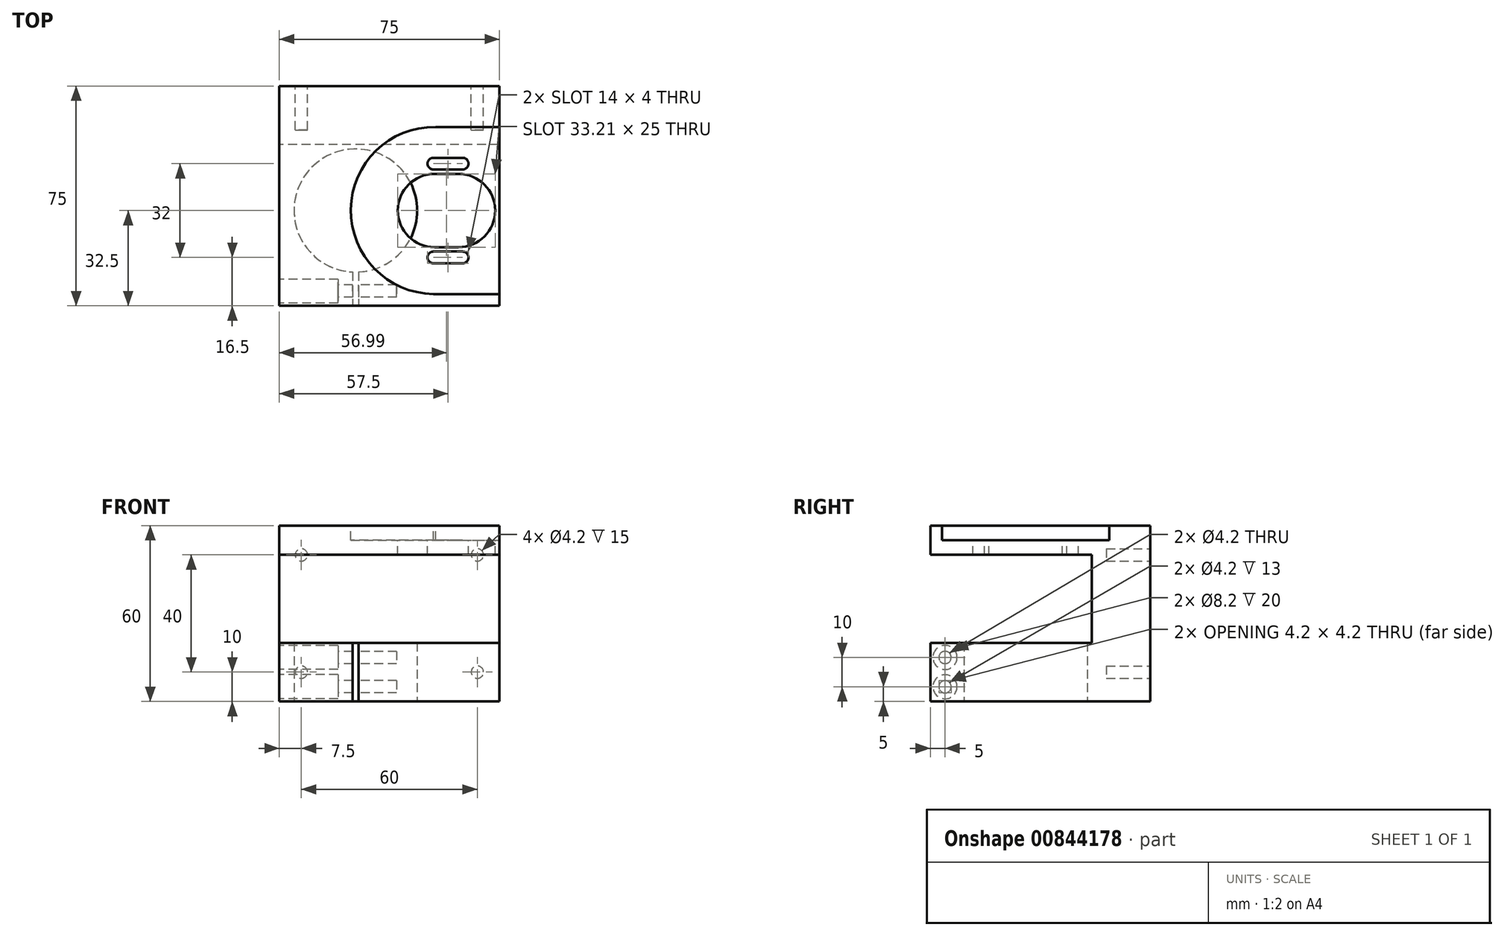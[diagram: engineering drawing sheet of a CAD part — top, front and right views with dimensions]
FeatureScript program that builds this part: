
annotation { "Feature Type Name" : "Feature", "Feature Type Description" : "" }
export const myFeature = defineFeature(function(context is Context, id is Id, definition is map)
    precondition{}
    {
        {
            var Q0;
            Q0=qCreatedBy(makeId("Top.planeOp"),FACE);
            var sketch = newSketch(context, id + "F0", { "sketchPlane" : qUnion([Q0])});
            skLineSegment(sketch, "E0.bottom", {"start": v(37.5, -37.5) * mm, "end": v(-37.5, -37.5) * mm});
            skLineSegment(sketch, "E0.top", {"start": v(37.5, 37.5) * mm, "end": v(-37.5, 37.5) * mm});
            skLineSegment(sketch, "E0.left", {"start": v(37.5, -37.5) * mm, "end": v(37.5, 37.5) * mm});
            skLineSegment(sketch, "E0.right", {"start": v(-37.5, -37.5) * mm, "end": v(-37.5, 37.5) * mm});
            skPoint(sketch, "E0.middle", {"position": v(0, 0) * mm});
            skLineSegment(sketch, "E1", {"start": v(-37.5, 0) * mm, "end": v(37.5, 0) * mm, "construction": true});
            skSolve(sketch);
        }
        {
            var Q0;
            Q0=makeQuery(id+"F0.imprint","IMPRINT",FACE,{"disambiguationData":[TD([[makeQuery(id+"F0.imprint","IMPRINT",EDGE,{"derivedFrom":sQuery(id+"F0.wireOp",EDGE,"E0.bottom")}),-1.0]])]});
            extrude(context, id + "F1", {"entities" : qUnion([Q0]), "depth" : 60 * mm, "offsetDistance" : 25 * mm});
        }
        {
            var Q0;
            Q0=makeQuery(id+"F1.opExtrude","SWEPT_FACE",FACE,{"disambiguationData":[OSD([sQuery(id+"F0.wireOp",EDGE,"E0.right")])]});
            var sketch = newSketch(context, id + "F2", { "sketchPlane" : qUnion([Q0])});
            skLineSegment(sketch, "E2.bottom", {"start": v(-17.5, 20) * mm, "end": v(40.42, 20) * mm});
            skLineSegment(sketch, "E2.top", {"start": v(-17.5, 50) * mm, "end": v(40.42, 50) * mm});
            skLineSegment(sketch, "E2.left", {"start": v(-17.5, 20) * mm, "end": v(-17.5, 50) * mm});
            skLineSegment(sketch, "E2.right", {"start": v(40.42, 20) * mm, "end": v(40.42, 50) * mm});
            skSolve(sketch);
        }
        {
            var Q0;
            {var subQ0=sQuery(id+"F2.wireOp",EDGE,"E2.left");Q0=makeQuery(id+"F2.imprint","IMPRINT",FACE,{"disambiguationData":[TD([[makeQuery(id+"F2.imprint","IMPRINT",EDGE,{"derivedFrom":subQ0}),-1.0]])]});}
            extrude(context, id + "F3", {"entities" : qUnion([Q0]), "operationType" : NewBodyOperationType.REMOVE, "endBound" : BoundingType.THROUGH_ALL, "oppositeDirection" : true, "depth" : 25 * mm, "offsetDistance" : 25 * mm});
        }
        {
            var Q0;
            Q0=makeQuery(id+"F1.opExtrude","CAP_FACE",FACE,{"disambiguationData":[OSD([sQuery(id+"F0.wireOp",EDGE,"E0.bottom"),sQuery(id+"F0.wireOp",EDGE,"E0.top"),sQuery(id+"F0.wireOp",EDGE,"E0.left"),sQuery(id+"F0.wireOp",EDGE,"E0.right")])],"isStart":true});
            var sketch = newSketch(context, id + "F4", { "sketchPlane" : qUnion([Q0])});
            skArc(sketch, "E3", {"start": v(-12.5, 25.98) * mm, "mid": v(-11.5, -16) * mm, "end": v(-10.5, 25.98) * mm});
            skLineSegment(sketch, "E4", {"start": v(-11.5, 5) * mm, "end": v(-11.5, 46.8) * mm, "construction": true});
            skLineSegment(sketch, "E5.top", {"start": v(-10.5, 41.66) * mm, "end": v(-12.5, 41.66) * mm});
            skLineSegment(sketch, "E5.left", {"start": v(-10.5, 25.98) * mm, "end": v(-10.5, 41.66) * mm});
            skLineSegment(sketch, "E5.right", {"start": v(-12.5, 25.98) * mm, "end": v(-12.5, 41.66) * mm});
            skPoint(sketch, "E5.middle", {"position": v(-11.5, 31.6) * mm});
            skPoint(sketch, "E6.orphan", {"position": v(-10.5, 21.54) * mm});
            skPoint(sketch, "E5.bottom.end.orphan", {"position": v(-12.5, 21.54) * mm});
            skSolve(sketch);
        }
        {
            var Q0;
            {var subQ0=sQuery(id+"F4.wireOp",EDGE,"E3");Q0=makeQuery(id+"F4.imprint","IMPRINT",FACE,{"disambiguationData":[TD([[makeQuery(id+"F4.imprint","IMPRINT",EDGE,{"derivedFrom":subQ0}),1.0]])]});}
            extrude(context, id + "F5", {"entities" : qUnion([Q0]), "operationType" : NewBodyOperationType.REMOVE, "oppositeDirection" : true, "depth" : 25 * mm, "offsetDistance" : 25 * mm});
        }
        {
            var Q0;
            Q0=makeQuery(id+"F1.opExtrude","SWEPT_FACE",FACE,{"disambiguationData":[OSD([sQuery(id+"F0.wireOp",EDGE,"E0.right")])]});
            var sketch = newSketch(context, id + "F6", { "sketchPlane" : qUnion([Q0])});
            skLineSegment(sketch, "E7", {"start": v(32.5, 20) * mm, "end": v(32.5, 0) * mm, "construction": true});
            skCircle(sketch, "E8", {"center": v(32.5, 15) * mm, "radius": 2.1 * mm});
            skCircle(sketch, "E9", {"center": v(32.5, 5) * mm, "radius": 2.1 * mm});
            skLineSegment(sketch, "E10", {"start": v(37.5, 10) * mm, "end": v(22, 10) * mm, "construction": true});
            skPoint(sketch, "E10.endSnap0", {"position": v(32.5, 10) * mm});
            skSolve(sketch);
        }
        {
            var Q0;
            Q0 = qSketchRegion(id + "F6", true);
            extrude(context, id + "F7", {"entities" : qUnion([Q0]), "operationType" : NewBodyOperationType.REMOVE, "oppositeDirection" : true, "depth" : 40 * mm, "offsetDistance" : 25 * mm});
        }
        {
            var Q0;
            Q0=makeQuery(id+"F1.opExtrude","SWEPT_FACE",FACE,{"disambiguationData":[OSD([sQuery(id+"F0.wireOp",EDGE,"E0.right")])]});
            var sketch = newSketch(context, id + "F8", { "sketchPlane" : qUnion([Q0])});
            skCircle(sketch, "E11", {"center": v(32.5, 15) * mm, "radius": 4.1 * mm});
            skCircle(sketch, "E12", {"center": v(32.5, 5) * mm, "radius": 4.1 * mm});
            skSolve(sketch);
        }
        {
            var Q0;
            Q0=makeQuery(id+"F8.imprint","IMPRINT",FACE,{"disambiguationData":[TD([[makeQuery(id+"F8.imprint","IMPRINT",EDGE,{"derivedFrom":sQuery(id+"F8.wireOp",EDGE,"E11")}),1.0]])]});
            var Q1;
            Q1=makeQuery(id+"F8.imprint","IMPRINT",FACE,{"disambiguationData":[TD([[makeQuery(id+"F8.imprint","IMPRINT",EDGE,{"derivedFrom":sQuery(id+"F8.wireOp",EDGE,"E12")}),1.0]])]});
            extrude(context, id + "F9", {"entities" : qUnion([Q0, Q1]), "operationType" : NewBodyOperationType.REMOVE, "oppositeDirection" : true, "depth" : 20 * mm, "offsetDistance" : 25 * mm});
        }
        {
            var Q0;
            Q0=makeQuery(id+"F1.opExtrude","CAP_FACE",FACE,{"disambiguationData":[OSD([sQuery(id+"F0.wireOp",EDGE,"E0.bottom"),sQuery(id+"F0.wireOp",EDGE,"E0.top"),sQuery(id+"F0.wireOp",EDGE,"E0.left"),sQuery(id+"F0.wireOp",EDGE,"E0.right")])],"isStart":false});
            var sketch = newSketch(context, id + "F10", { "sketchPlane" : qUnion([Q0])});
            skLineSegment(sketch, "E13", {"start": v(-1.64, -5) * mm, "end": v(42.67, -5) * mm, "construction": true});
            skLineSegment(sketch, "E14", {"start": v(20, 7.06) * mm, "end": v(20, -13.87) * mm, "construction": true});
            skLineSegment(sketch, "E15", {"start": v(15, 11) * mm, "end": v(25, 11) * mm});
            skLineSegment(sketch, "E16", {"start": v(15, -21) * mm, "end": v(25, -21) * mm});
            skArc(sketch, "E17.0.startCap", {"start": v(15, 9) * mm, "mid": v(13, 11) * mm, "end": v(15, 13) * mm});
            skArc(sketch, "E17.0.endCap", {"start": v(25, 13) * mm, "mid": v(27, 11) * mm, "end": v(25, 9) * mm});
            skLineSegment(sketch, "E17.0.left", {"start": v(15, 13) * mm, "end": v(25, 13) * mm});
            skLineSegment(sketch, "E17.0.right", {"start": v(15, 9) * mm, "end": v(25, 9) * mm});
            skArc(sketch, "E18.0.startCap", {"start": v(15, -23) * mm, "mid": v(13, -21) * mm, "end": v(15, -19) * mm});
            skArc(sketch, "E18.0.endCap", {"start": v(25, -19) * mm, "mid": v(27, -21) * mm, "end": v(25, -23) * mm});
            skLineSegment(sketch, "E18.0.left", {"start": v(15, -19) * mm, "end": v(25, -19) * mm});
            skLineSegment(sketch, "E18.0.right", {"start": v(15, -23) * mm, "end": v(25, -23) * mm});
            skArc(sketch, "E19", {"start": v(23.6, -17.5) * mm, "mid": v(36.1, -5) * mm, "end": v(23.6, 7.5) * mm});
            skLineSegment(sketch, "E20", {"start": v(15.38, 7.5) * mm, "end": v(23.6, 7.5) * mm});
            skLineSegment(sketch, "E21", {"start": v(15.38, -17.5) * mm, "end": v(23.6, -17.5) * mm});
            skArc(sketch, "E22.trimOffspring", {"start": v(15.38, 7.5) * mm, "mid": v(2.88, -5) * mm, "end": v(15.38, -17.5) * mm});
            skSolve(sketch);
        }
        {
            var Q0;
            Q0 = qSketchRegion(id + "F10", true);
            extrude(context, id + "F11", {"entities" : qUnion([Q0]), "operationType" : NewBodyOperationType.REMOVE, "oppositeDirection" : true, "depth" : 25 * mm, "offsetDistance" : 25 * mm});
        }
        {
            var Q0;
            Q0=makeQuery(id+"F1.opExtrude","CAP_FACE",FACE,{"disambiguationData":[OSD([sQuery(id+"F0.wireOp",EDGE,"E0.bottom"),sQuery(id+"F0.wireOp",EDGE,"E0.top"),sQuery(id+"F0.wireOp",EDGE,"E0.left"),sQuery(id+"F0.wireOp",EDGE,"E0.right")])],"isStart":false});
            var sketch = newSketch(context, id + "F12", { "sketchPlane" : qUnion([Q0])});
            skArc(sketch, "E23", {"start": v(15.77, 23.5) * mm, "mid": v(-13.11, -4.62) * mm, "end": v(15, -33.5) * mm});
            skLineSegment(sketch, "E24.bottom", {"start": v(15, 23.5) * mm, "end": v(72, 23.5) * mm});
            skLineSegment(sketch, "E24.top", {"start": v(15, -33.5) * mm, "end": v(72, -33.5) * mm});
            skLineSegment(sketch, "E24.left", {"start": v(15, -33.5) * mm, "end": v(15, -33.5) * mm});
            skLineSegment(sketch, "E24.right", {"start": v(72, 23.5) * mm, "end": v(72, -33.5) * mm});
            skSolve(sketch);
        }
        {
            var Q0;
            Q0 = qSketchRegion(id + "F12", true);
            extrude(context, id + "F13", {"entities" : qUnion([Q0]), "operationType" : NewBodyOperationType.REMOVE, "oppositeDirection" : true, "depth" : 5 * mm, "offsetDistance" : 25 * mm});
        }
        {
            var Q0;
            Q0=makeQuery(id+"F1.opExtrude","SWEPT_FACE",FACE,{"disambiguationData":[OSD([sQuery(id+"F0.wireOp",EDGE,"E0.top")])]});
            var sketch = newSketch(context, id + "F14", { "sketchPlane" : qUnion([Q0])});
            skLineSegment(sketch, "E25", {"start": v(0, 60) * mm, "end": v(0, 0) * mm, "construction": true});
            skLineSegment(sketch, "E26.bottom", {"start": v(30, 10) * mm, "end": v(-30, 10) * mm, "construction": true});
            skLineSegment(sketch, "E26.top", {"start": v(30, 50) * mm, "end": v(-30, 50) * mm, "construction": true});
            skLineSegment(sketch, "E26.left", {"start": v(30, 10) * mm, "end": v(30, 50) * mm, "construction": true});
            skLineSegment(sketch, "E26.right", {"start": v(-30, 10) * mm, "end": v(-30, 50) * mm, "construction": true});
            skPoint(sketch, "E26.middle", {"position": v(0, 30) * mm});
            skCircle(sketch, "E27", {"center": v(-30, 50) * mm, "radius": 2.1 * mm});
            skCircle(sketch, "E28", {"center": v(30, 50) * mm, "radius": 2.1 * mm});
            skCircle(sketch, "E29", {"center": v(30, 10) * mm, "radius": 2.1 * mm});
            skCircle(sketch, "E30", {"center": v(-30, 10) * mm, "radius": 2.1 * mm});
            skSolve(sketch);
        }
        {
            var Q0;
            Q0 = qSketchRegion(id + "F14", true);
            extrude(context, id + "F15", {"entities" : qUnion([Q0]), "operationType" : NewBodyOperationType.REMOVE, "oppositeDirection" : true, "depth" : 15 * mm, "offsetDistance" : 25 * mm});
        }
    });
